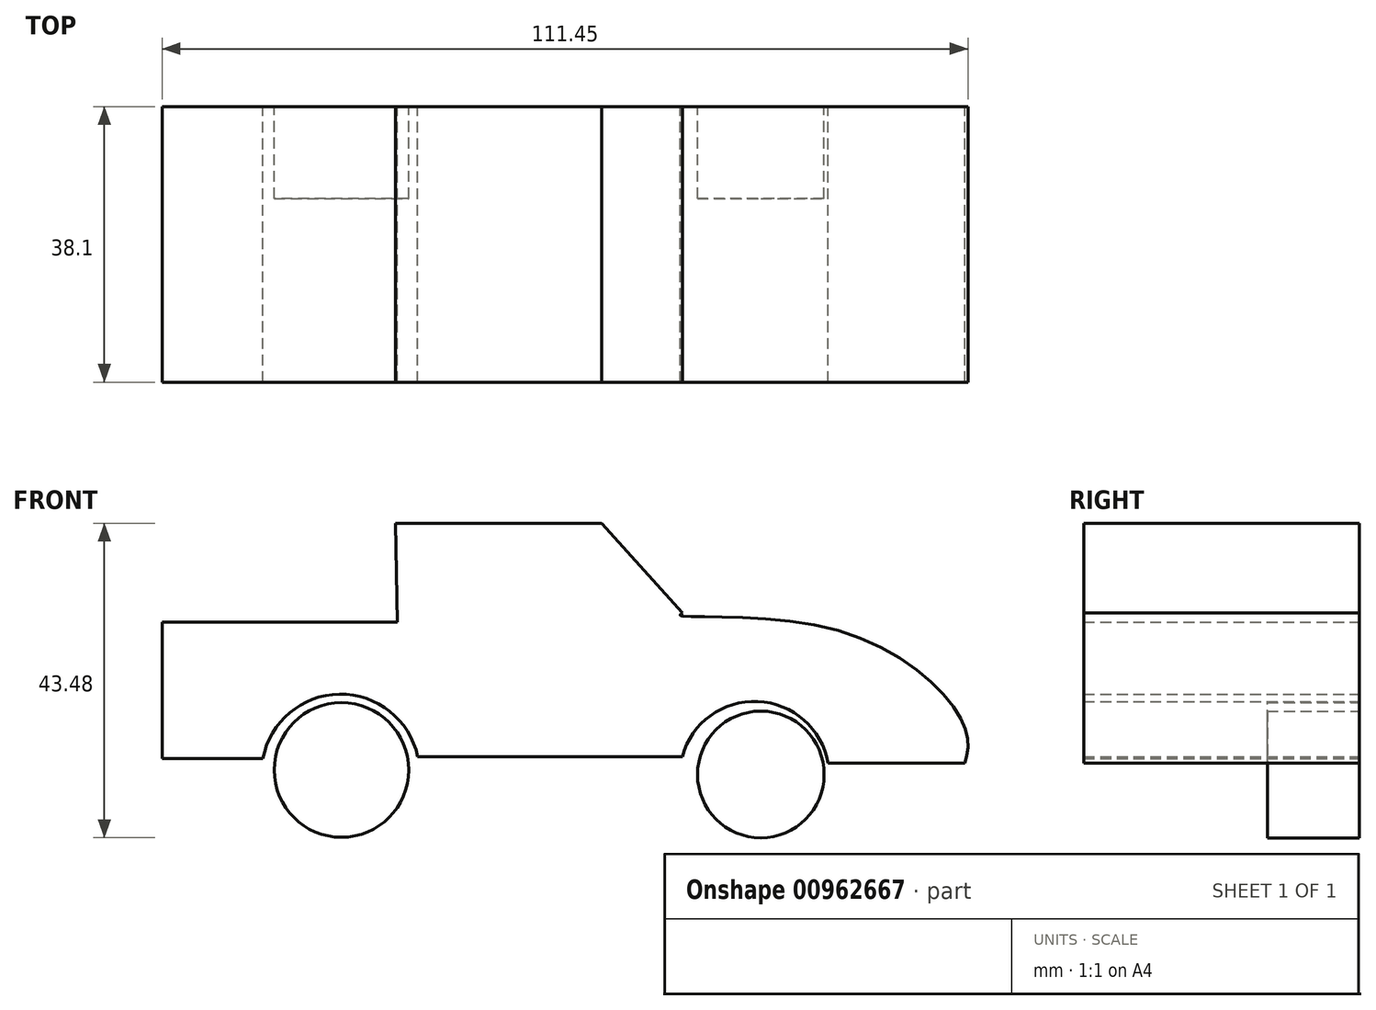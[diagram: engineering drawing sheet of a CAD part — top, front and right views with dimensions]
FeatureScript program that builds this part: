
annotation { "Feature Type Name" : "Feature", "Feature Type Description" : "" }
export const myFeature = defineFeature(function(context is Context, id is Id, definition is map)
    precondition{}
    {
        {
            var Q0;
            Q0=qCreatedBy(makeId("Front.planeOp"),FACE);
            var sketch = newSketch(context, id + "F0", { "sketchPlane" : qUnion([Q0])});
            skLineSegment(sketch, "E0", {"start": v(-75.82, 10.08) * mm, "end": v(-75.82, -8.84) * mm});
            skLineSegment(sketch, "E1", {"start": v(-75.82, -8.84) * mm, "end": v(-61.87, -8.84) * mm});
            skLineSegment(sketch, "E2", {"start": v(-40.47, -8.53) * mm, "end": v(-3.88, -8.53) * mm});
            skArc(sketch, "E3", {"start": v(-40.47, -8.53) * mm, "mid": v(-51.3, 0.09) * mm, "end": v(-61.87, -8.84) * mm});
            skLineSegment(sketch, "E4", {"start": v(16.28, -9.46) * mm, "end": v(35.2, -9.46) * mm});
            skArc(sketch, "E5", {"start": v(16.28, -9.46) * mm, "mid": v(6.57, -0.92) * mm, "end": v(-3.88, -8.53) * mm});
            skFitSpline(sketch, "E6", {"points": [v(35.2, -9.46) * mm, v(35.2, -4.5) * mm, v(17.83, 8.84) * mm, v(-4.19, 11) * mm, v(-3.88, 11.32) * mm], "startDerivative": vector(6.14, 24.51) * mm, "endDerivative": vector(10.11, 6.37) * mm});
            skLineSegment(sketch, "E7", {"start": v(-75.82, 10.08) * mm, "end": v(-43.26, 10.08) * mm});
            skLineSegment(sketch, "E8", {"start": v(-3.88, 11.32) * mm, "end": v(-15.04, 23.72) * mm});
            skLineSegment(sketch, "E9", {"start": v(-15.04, 23.72) * mm, "end": v(-43.57, 23.72) * mm});
            skLineSegment(sketch, "E10", {"start": v(-43.57, 23.72) * mm, "end": v(-43.26, 10.08) * mm});
            skSolve(sketch);
        }
        {
            var Q0;
            Q0 = qSketchRegion(id + "F0", true);
            extrude(context, id + "F1", {"entities" : qUnion([Q0]), "depth" : 38.1 * mm, "offsetDistance" : 25.4 * mm});
        }
        {
            var Q0;
            Q0=qCreatedBy(makeId("Front.planeOp"),FACE);
            var sketch = newSketch(context, id + "F2", { "sketchPlane" : qUnion([Q0])});
            skCircle(sketch, "E11", {"center": v(-51.01, -10.39) * mm, "radius": 9.3 * mm});
            skCircle(sketch, "E12", {"center": v(6.98, -11) * mm, "radius": 8.75 * mm});
            skSolve(sketch);
        }
        {
            var Q0;
            Q0=makeQuery(id+"F2.imprint","IMPRINT",FACE,{"disambiguationData":[TD([[makeQuery(id+"F2.imprint","IMPRINT",EDGE,{"derivedFrom":sQuery(id+"F2.wireOp",EDGE,"E12")}),1.0]])]});
            var Q1;
            Q1=makeQuery(id+"F2.imprint","IMPRINT",FACE,{"disambiguationData":[TD([[makeQuery(id+"F2.imprint","IMPRINT",EDGE,{"derivedFrom":sQuery(id+"F2.wireOp",EDGE,"E11")}),1.0]])]});
            extrude(context, id + "F3", {"entities" : qUnion([Q0, Q1]), "depth" : 12.7 * mm, "offsetDistance" : 25.4 * mm});
        }
    });
